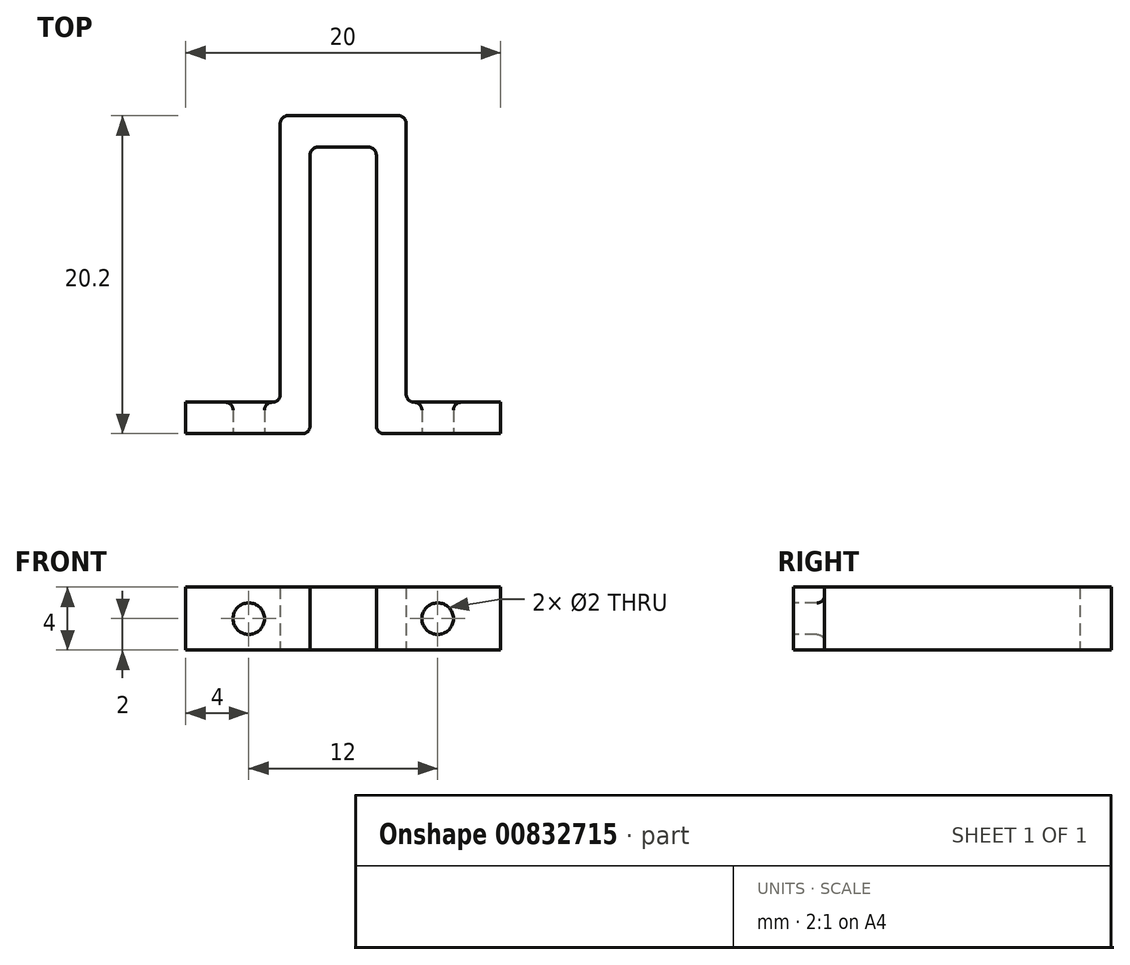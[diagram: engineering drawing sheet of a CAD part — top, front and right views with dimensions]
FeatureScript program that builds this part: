
annotation { "Feature Type Name" : "Feature", "Feature Type Description" : "" }
export const myFeature = defineFeature(function(context is Context, id is Id, definition is map)
    precondition{}
    {
        {
            var Q0;
            Q0=qCreatedBy(makeId("Top.planeOp"),FACE);
            var sketch = newSketch(context, id + "F0", { "sketchPlane" : qUnion([Q0])});
            skLineSegment(sketch, "E0", {"start": v(0, 0) * mm, "end": v(7.9, 0) * mm});
            skLineSegment(sketch, "E1", {"start": v(20, 0) * mm, "end": v(20, 2) * mm});
            skLineSegment(sketch, "E2", {"start": v(0, 0) * mm, "end": v(0, 2) * mm});
            skLineSegment(sketch, "E3", {"start": v(4, 0) * mm, "end": v(4, 15.02) * mm, "construction": true});
            skLineSegment(sketch, "E4", {"start": v(16, 0) * mm, "end": v(16, 14.92) * mm, "construction": true});
            skLineSegment(sketch, "E5", {"start": v(0, 2) * mm, "end": v(6, 2) * mm});
            skLineSegment(sketch, "E6", {"start": v(20, 2) * mm, "end": v(14, 2) * mm});
            skLineSegment(sketch, "E7.0", {"start": v(5, 0) * mm, "end": v(5, 15.02) * mm, "construction": true});
            skLineSegment(sketch, "E8", {"start": v(6, 2) * mm, "end": v(6, 20.2) * mm});
            skLineSegment(sketch, "E9", {"start": v(14, 2) * mm, "end": v(14, 20.2) * mm});
            skLineSegment(sketch, "E10.0", {"start": v(15, 0) * mm, "end": v(15, 14.92) * mm, "construction": true});
            skLineSegment(sketch, "E11", {"start": v(6, 20.2) * mm, "end": v(14, 20.2) * mm});
            skLineSegment(sketch, "E12.0", {"start": v(7.9, 0) * mm, "end": v(7.9, 18.2) * mm});
            skLineSegment(sketch, "E13.0", {"start": v(7.9, 18.2) * mm, "end": v(12.1, 18.2) * mm});
            skLineSegment(sketch, "E14.0", {"start": v(12.1, 0) * mm, "end": v(12.1, 18.2) * mm});
            skLineSegment(sketch, "E15.trimOffspring", {"start": v(12.1, 0) * mm, "end": v(20, 0) * mm});
            skSolve(sketch);
        }
        {
            var Q0;
            Q0=qCreatedBy(makeId("Front.planeOp"),FACE);
            var sketch = newSketch(context, id + "F1", { "sketchPlane" : qUnion([Q0])});
            skPoint(sketch, "E16", {"position": v(4, 0) * mm});
            skPoint(sketch, "E17", {"position": v(16, 0) * mm});
            skPoint(sketch, "E18", {"position": v(0, 2) * mm});
            skLineSegment(sketch, "E19", {"start": v(4, 0) * mm, "end": v(4, 5.77) * mm, "construction": true});
            skLineSegment(sketch, "E20", {"start": v(16, 0) * mm, "end": v(16, 5.8) * mm, "construction": true});
            skLineSegment(sketch, "E21", {"start": v(0, 2) * mm, "end": v(18.78, 2) * mm, "construction": true});
            skCircle(sketch, "E22", {"center": v(4, 2) * mm, "radius": 1 * mm});
            skCircle(sketch, "E23", {"center": v(16, 2) * mm, "radius": 1 * mm});
            skSolve(sketch);
        }
        {
            var Q0;
            Q0=makeQuery(id+"F0.imprint","IMPRINT",FACE,{"disambiguationData":[TD([[makeQuery(id+"F0.imprint","IMPRINT",EDGE,{"derivedFrom":sQuery(id+"F0.wireOp",EDGE,"E0")}),1.0]])]});
            extrude(context, id + "F2", {"entities" : qUnion([Q0]), "depth" : 4 * mm, "offsetDistance" : 25 * mm});
        }
        {
            var Q0;
            Q0=makeQuery(id+"F1.imprint","IMPRINT",FACE,{"disambiguationData":[TD([[makeQuery(id+"F1.imprint","IMPRINT",EDGE,{"derivedFrom":sQuery(id+"F1.wireOp",EDGE,"E22")}),1.0]])]});
            var Q1;
            Q1=makeQuery(id+"F1.imprint","IMPRINT",FACE,{"disambiguationData":[TD([[makeQuery(id+"F1.imprint","IMPRINT",EDGE,{"derivedFrom":sQuery(id+"F1.wireOp",EDGE,"E23")}),1.0]])]});
            extrude(context, id + "F3", {"entities" : qUnion([Q0, Q1]), "oppositeDirection" : true, "depth" : 22.2 * mm, "offsetDistance" : 25 * mm});
        }
        {
            var Q0;
            Q0=makeQuery(id+"F3.opExtrude","SWEPT_BODY",BODY,{"disambiguationData":[OSD([sQuery(id+"F1.wireOp",EDGE,"E22")])]});
            var Q1;
            Q1=makeQuery(id+"F3.opExtrude","SWEPT_BODY",BODY,{"disambiguationData":[OSD([sQuery(id+"F1.wireOp",EDGE,"E23")])]});
            var Q2;
            Q2=makeQuery(id+"F2.opExtrude","SWEPT_BODY",BODY,{"disambiguationData":[OSD([sQuery(id+"F0.wireOp",EDGE,"E0"),sQuery(id+"F0.wireOp",EDGE,"E1"),sQuery(id+"F0.wireOp",EDGE,"E2"),sQuery(id+"F0.wireOp",EDGE,"E5"),sQuery(id+"F0.wireOp",EDGE,"E6"),sQuery(id+"F0.wireOp",EDGE,"E8"),sQuery(id+"F0.wireOp",EDGE,"E9"),sQuery(id+"F0.wireOp",EDGE,"E11"),sQuery(id+"F0.wireOp",EDGE,"E12.0"),sQuery(id+"F0.wireOp",EDGE,"E13.0"),sQuery(id+"F0.wireOp",EDGE,"E14.0"),sQuery(id+"F0.wireOp",EDGE,"E15.trimOffspring")])]});
            booleanBodies(context, id + "F4", {"operationType" : BooleanOperationType.SUBTRACTION, "tools" : qUnion([Q0, Q1]), "targets" : qUnion([Q2])});
        }
        {
            var Q0;
            Q0=makeQuery(id+"F2.opExtrude","SWEPT_EDGE",EDGE,{"disambiguationData":[OSD([sQuery(id+"F0.wireOp",EDGE,"E0"),sQuery(id+"F0.wireOp",EDGE,"E12.0")])]});
            var Q1;
            Q1=makeQuery(id+"F2.opExtrude","SWEPT_EDGE",EDGE,{"disambiguationData":[OSD([sQuery(id+"F0.wireOp",EDGE,"E14.0"),sQuery(id+"F0.wireOp",EDGE,"E15.trimOffspring")])]});
            var Q2;
            Q2=makeQuery(id+"F2.opExtrude","SWEPT_EDGE",EDGE,{"disambiguationData":[OSD([sQuery(id+"F0.wireOp",EDGE,"E9"),sQuery(id+"F0.wireOp",EDGE,"E11")])]});
            var Q3;
            Q3=makeQuery(id+"F2.opExtrude","SWEPT_EDGE",EDGE,{"disambiguationData":[OSD([sQuery(id+"F0.wireOp",EDGE,"E12.0"),sQuery(id+"F0.wireOp",EDGE,"E13.0")])]});
            var Q4;
            Q4=makeQuery(id+"F2.opExtrude","SWEPT_EDGE",EDGE,{"disambiguationData":[OSD([sQuery(id+"F0.wireOp",EDGE,"E13.0"),sQuery(id+"F0.wireOp",EDGE,"E14.0")])]});
            var Q5;
            Q5=makeQuery(id+"F2.opExtrude","SWEPT_EDGE",EDGE,{"disambiguationData":[OSD([sQuery(id+"F0.wireOp",EDGE,"E8"),sQuery(id+"F0.wireOp",EDGE,"E11")])]});
            var Q6;
            Q6=makeQuery(id+"F2.opExtrude","SWEPT_EDGE",EDGE,{"disambiguationData":[OSD([sQuery(id+"F0.wireOp",EDGE,"E5"),sQuery(id+"F0.wireOp",EDGE,"E8")])]});
            var Q7;
            Q7=makeQuery(id+"F2.opExtrude","SWEPT_EDGE",EDGE,{"disambiguationData":[OSD([sQuery(id+"F0.wireOp",EDGE,"E6"),sQuery(id+"F0.wireOp",EDGE,"E9")])]});
            var Q8;
            Q8=makeQuery(id+"F4.opBoolean","INTERSECT",EDGE,{"derivedFrom":[makeQuery(id+"F2.opExtrude","SWEPT_FACE",FACE,{"disambiguationData":[OSD([sQuery(id+"F0.wireOp",EDGE,"E5")])]}),makeQuery(id+"F3.opExtrude","SWEPT_FACE",FACE,{"disambiguationData":[OSD([sQuery(id+"F1.wireOp",EDGE,"E22")])]})]});
            var Q9;
            Q9=makeQuery(id+"F4.opBoolean","INTERSECT",EDGE,{"derivedFrom":[makeQuery(id+"F2.opExtrude","SWEPT_FACE",FACE,{"disambiguationData":[OSD([sQuery(id+"F0.wireOp",EDGE,"E6")])]}),makeQuery(id+"F3.opExtrude","SWEPT_FACE",FACE,{"disambiguationData":[OSD([sQuery(id+"F1.wireOp",EDGE,"E23")])]})]});
            var Q10;
            Q10=makeQuery(id+"F4.opBoolean","COPY",EDGE,{"derivedFrom":makeQuery(id+"F3.opExtrude","CAP_EDGE",EDGE,{"disambiguationData":[OSD([sQuery(id+"F1.wireOp",EDGE,"E22")])],"isStart":true})});
            var Q11;
            Q11=makeQuery(id+"F4.opBoolean","COPY",EDGE,{"derivedFrom":makeQuery(id+"F3.opExtrude","CAP_EDGE",EDGE,{"disambiguationData":[OSD([sQuery(id+"F1.wireOp",EDGE,"E23")])],"isStart":true})});
            fillet(context, id + "F5", {"entities" : qUnion([Q0, Q1, Q2, Q3, Q4, Q5, Q6, Q7, Q8, Q9, Q10, Q11]), "radius" : 0.5 * mm, "tangentPropagation" : true, "allowEdgeOverflow" : false});
        }
    });
